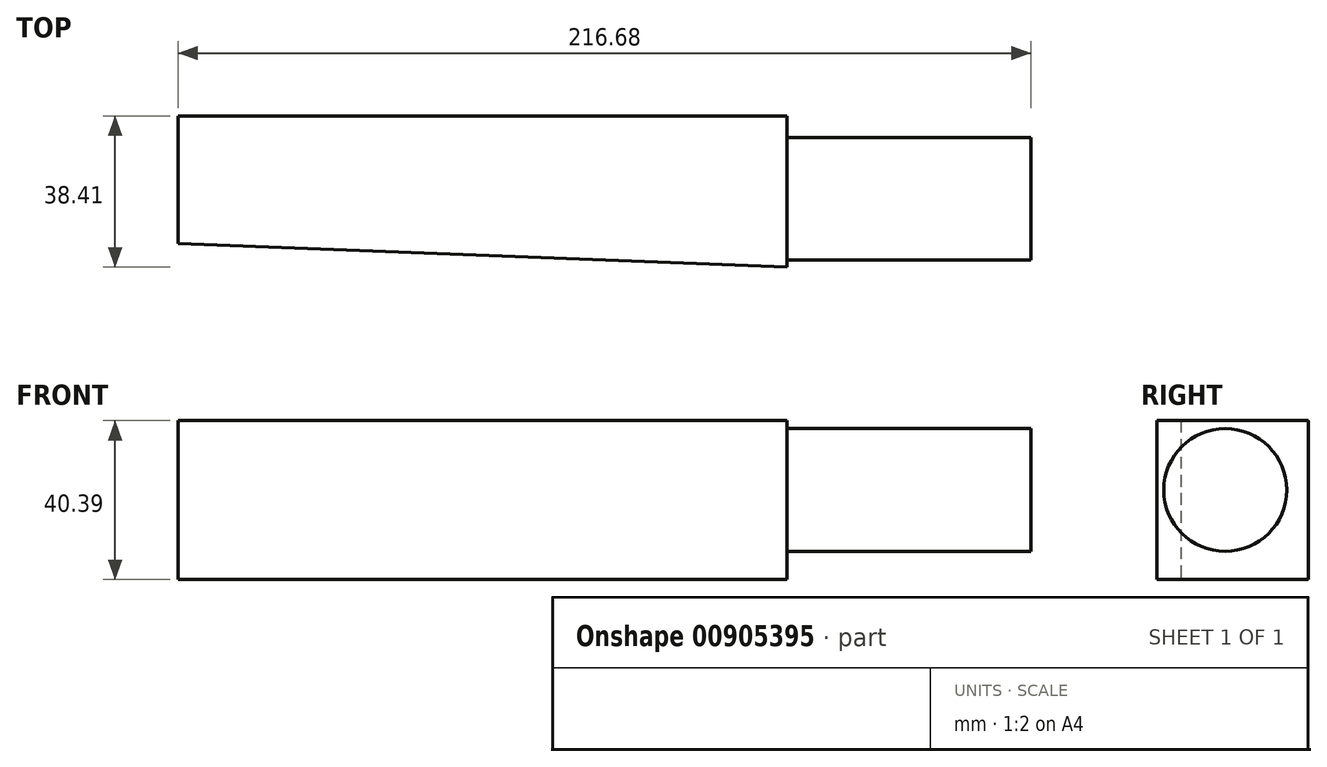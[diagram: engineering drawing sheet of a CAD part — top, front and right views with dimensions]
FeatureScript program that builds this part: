
annotation { "Feature Type Name" : "Feature", "Feature Type Description" : "" }
export const myFeature = defineFeature(function(context is Context, id is Id, definition is map)
    precondition{}
    {
        {
            var Q0;
            Q0=qCreatedBy(makeId("Top.planeOp"),FACE);
            var sketch = newSketch(context, id + "F0", { "sketchPlane" : qUnion([Q0])});
            skLineSegment(sketch, "E0", {"start": v(-75.81, 0) * mm, "end": v(78.9, 0) * mm});
            skLineSegment(sketch, "E1", {"start": v(-75.81, 0) * mm, "end": v(-75.81, -32.38) * mm});
            skLineSegment(sketch, "E2", {"start": v(-75.81, -32.38) * mm, "end": v(78.9, -38.4) * mm});
            skLineSegment(sketch, "E3", {"start": v(78.9, -38.4) * mm, "end": v(78.9, 0) * mm});
            skSolve(sketch);
        }
        {
            var Q0;
            Q0 = qSketchRegion(id + "F0", true);
            extrude(context, id + "F1", {"entities" : qUnion([Q0]), "depth" : 40.4 * mm, "offsetDistance" : 25.4 * mm});
        }
        {
            var Q0;
            Q0=makeQuery(id+"F1.opExtrude","SWEPT_FACE",FACE,{"disambiguationData":[OSD([sQuery(id+"F0.wireOp",EDGE,"E3")])]});
            var sketch = newSketch(context, id + "F2", { "sketchPlane" : qUnion([Q0])});
            skCircle(sketch, "E4", {"center": v(-21.06, 22.76) * mm, "radius": 15.6 * mm});
            skSolve(sketch);
        }
        {
            var Q0;
            Q0 = qSketchRegion(id + "F2", true);
            extrude(context, id + "F3", {"entities" : qUnion([Q0]), "operationType" : NewBodyOperationType.ADD, "depth" : 61.98 * mm, "offsetDistance" : 25.4 * mm});
        }
    });
